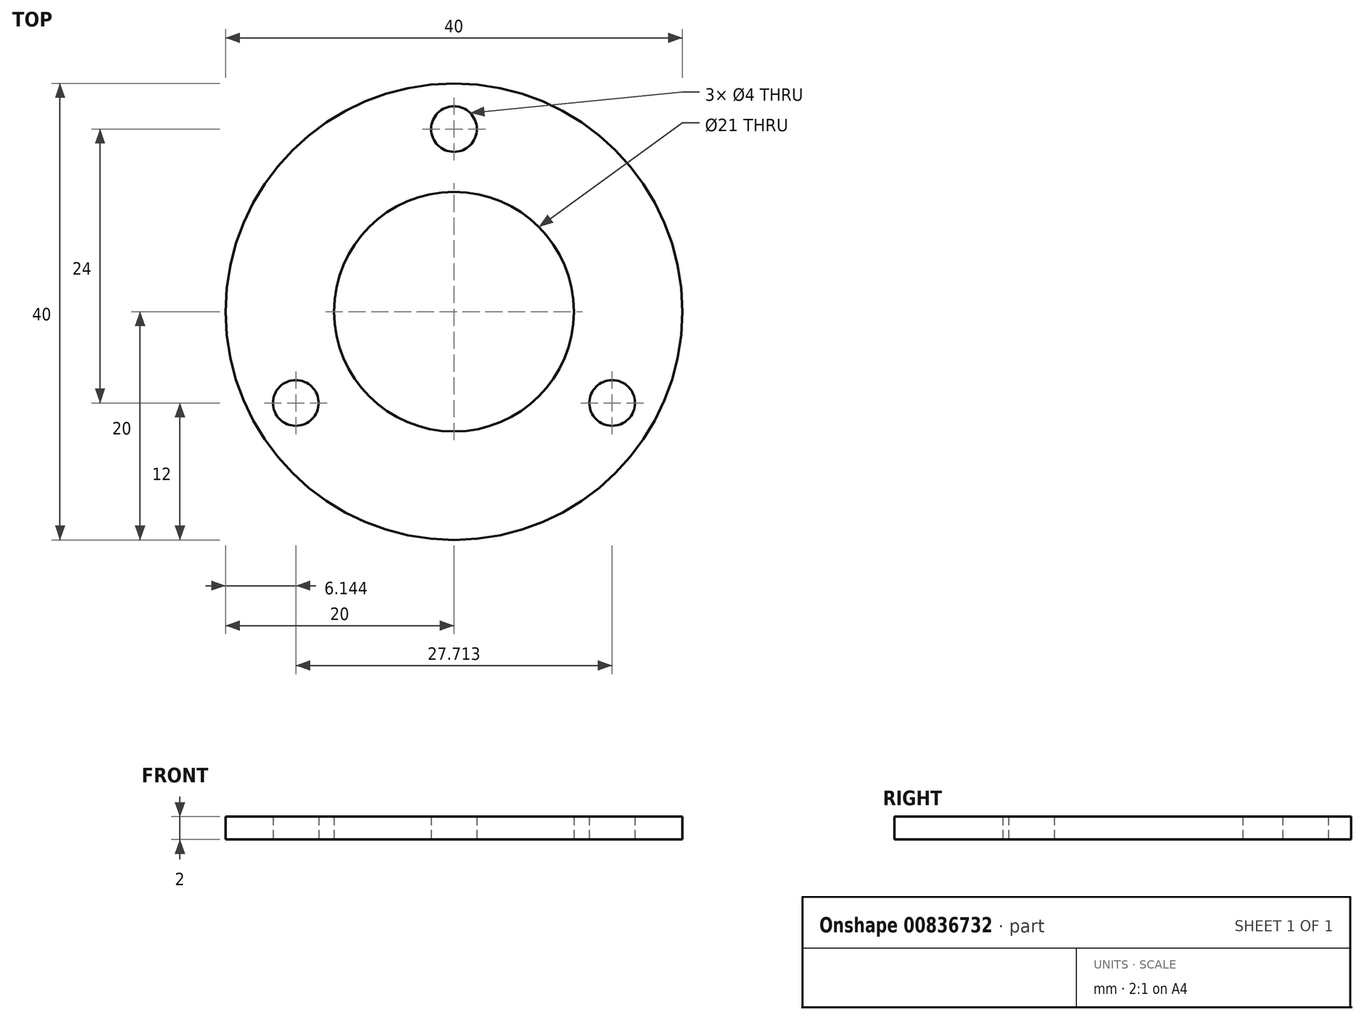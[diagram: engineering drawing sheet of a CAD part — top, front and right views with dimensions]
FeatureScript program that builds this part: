
annotation { "Feature Type Name" : "Feature", "Feature Type Description" : "" }
export const myFeature = defineFeature(function(context is Context, id is Id, definition is map)
    precondition{}
    {
        {
            var Q0;
            Q0=qCreatedBy(makeId("Top.planeOp"),FACE);
            var sketch = newSketch(context, id + "F0", { "sketchPlane" : qUnion([Q0])});
            skCircle(sketch, "E0", {"center": v(0, 0) * mm, "radius": 20 * mm});
            skCircle(sketch, "E1", {"center": v(0, 0) * mm, "radius": 16 * mm, "construction": true});
            skCircle(sketch, "E2", {"center": v(0, 16) * mm, "radius": 2 * mm});
            skLineSegment(sketch, "E3", {"start": v(0, 16) * mm, "end": v(-13.86, -8) * mm, "construction": true});
            skLineSegment(sketch, "E4", {"start": v(-13.86, -8) * mm, "end": v(13.86, -8) * mm, "construction": true});
            skLineSegment(sketch, "E5", {"start": v(13.86, -8) * mm, "end": v(0, 16) * mm, "construction": true});
            skCircle(sketch, "E6", {"center": v(-13.86, -8) * mm, "radius": 2 * mm});
            skCircle(sketch, "E7", {"center": v(13.86, -8) * mm, "radius": 2 * mm});
            skCircle(sketch, "E8", {"center": v(0, 0) * mm, "radius": 10.5 * mm});
            skSolve(sketch);
        }
        {
            var Q0;
            Q0=makeQuery(id+"F0.imprint","IMPRINT",FACE,{"disambiguationData":[TD([[makeQuery(id+"F0.imprint","IMPRINT",EDGE,{"derivedFrom":sQuery(id+"F0.wireOp",EDGE,"E0")}),1.0]])]});
            extrude(context, id + "F1", {"entities" : qUnion([Q0]), "depth" : 2 * mm, "offsetDistance" : 25 * mm});
        }
    });
